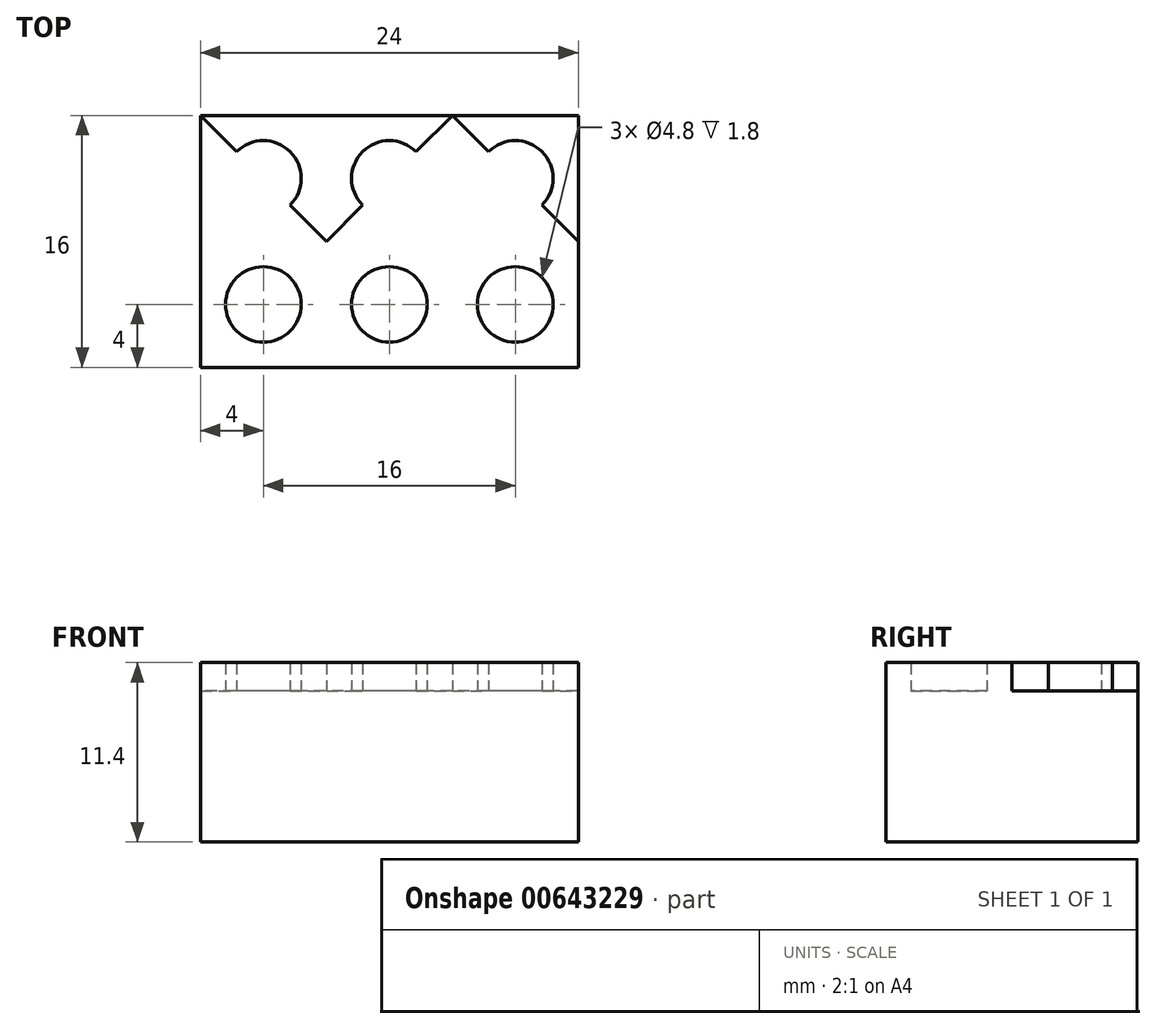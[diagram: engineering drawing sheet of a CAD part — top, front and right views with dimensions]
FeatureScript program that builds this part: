
annotation { "Feature Type Name" : "Feature", "Feature Type Description" : "" }
export const myFeature = defineFeature(function(context is Context, id is Id, definition is map)
    precondition{}
    {
        {
            var Q0;
            Q0=qCreatedBy(makeId("Top.planeOp"),FACE);
            var sketch = newSketch(context, id + "F0", { "sketchPlane" : qUnion([Q0])});
            skLineSegment(sketch, "E0.bottom", {"start": v(0, 0) * mm, "end": v(-24, 0) * mm});
            skLineSegment(sketch, "E0.top", {"start": v(0, 16) * mm, "end": v(-24, 16) * mm});
            skLineSegment(sketch, "E0.left", {"start": v(0, 0) * mm, "end": v(0, 16) * mm});
            skLineSegment(sketch, "E0.right", {"start": v(-24, 0) * mm, "end": v(-24, 16) * mm});
            skSolve(sketch);
        }
        {
            var Q0;
            Q0=makeQuery(id+"F0.imprint","IMPRINT",FACE,{"disambiguationData":[TD([[makeQuery(id+"F0.imprint","IMPRINT",EDGE,{"derivedFrom":sQuery(id+"F0.wireOp",EDGE,"E0.bottom")}),-1.0]])]});
            extrude(context, id + "F1", {"entities" : qUnion([Q0]), "depth" : 9.6 * mm, "offsetDistance" : 25.4 * mm});
        }
        {
            var Q0;
            Q0=makeQuery(id+"F1.opExtrude","CAP_FACE",FACE,{"disambiguationData":[OSD([sQuery(id+"F0.wireOp",EDGE,"E0.bottom"),sQuery(id+"F0.wireOp",EDGE,"E0.top"),sQuery(id+"F0.wireOp",EDGE,"E0.left"),sQuery(id+"F0.wireOp",EDGE,"E0.right")])],"isStart":false});
            var sketch = newSketch(context, id + "F2", { "sketchPlane" : qUnion([Q0])});
            skLineSegment(sketch, "E1", {"start": v(-24, 8) * mm, "end": v(0, 8) * mm, "construction": true});
            skLineSegment(sketch, "E2", {"start": v(-8, 16) * mm, "end": v(-8, 0) * mm, "construction": true});
            skLineSegment(sketch, "E3", {"start": v(-16, 16) * mm, "end": v(-16, 0) * mm, "construction": true});
            skLineSegment(sketch, "E4", {"start": v(-24, 16) * mm, "end": v(-16, 8) * mm});
            skLineSegment(sketch, "E5", {"start": v(-16, 8) * mm, "end": v(-8, 16) * mm});
            skLineSegment(sketch, "E6", {"start": v(-8, 16) * mm, "end": v(0, 8) * mm});
            skCircle(sketch, "E7", {"center": v(-20, 12) * mm, "radius": 2.4 * mm});
            skCircle(sketch, "E8", {"center": v(-12, 12) * mm, "radius": 2.4 * mm});
            skCircle(sketch, "E9", {"center": v(-4, 12) * mm, "radius": 2.4 * mm});
            skCircle(sketch, "E10.MirrorC", {"center": v(-20, 4) * mm, "radius": 2.4 * mm});
            skCircle(sketch, "E11.MirrorC", {"center": v(-12, 4) * mm, "radius": 2.4 * mm});
            skCircle(sketch, "E12.MirrorC", {"center": v(-4, 4) * mm, "radius": 2.4 * mm});
            skSolve(sketch);
        }
        {
            var Q0;
            {var subQ0=sQuery(id+"F2.wireOp",EDGE,"E7");var subQ1=sQuery(id+"F2.wireOp",EDGE,"E4");var subQ2=makeQuery(id+"F2.imprint","INTERSECT",VERTEX,{"disambiguationData":[OD(0.0)],"derivedFrom":[subQ1,subQ0]});Q0=makeQuery(id+"F2.imprint","IMPRINT",FACE,{"disambiguationData":[TD([[makeQuery(id+"F2.imprint","IMPRINT",EDGE,{"disambiguationData":[TD([[subQ2,-1.0]])],"derivedFrom":subQ1}),-1.0]])]});}
            var Q1;
            {var subQ0=sQuery(id+"F2.wireOp",EDGE,"E7");var subQ1=sQuery(id+"F2.wireOp",EDGE,"E4");var subQ2=makeQuery(id+"F2.imprint","INTERSECT",VERTEX,{"disambiguationData":[OD(0.0)],"derivedFrom":[subQ1,subQ0]});Q1=makeQuery(id+"F2.imprint","IMPRINT",FACE,{"disambiguationData":[TD([[makeQuery(id+"F2.imprint","IMPRINT",EDGE,{"disambiguationData":[TD([[subQ2,-1.0]])],"derivedFrom":subQ1}),1.0]])]});}
            var Q2;
            {var subQ0=sQuery(id+"F2.wireOp",EDGE,"E8");var subQ1=sQuery(id+"F2.wireOp",EDGE,"E5");var subQ2=makeQuery(id+"F2.imprint","INTERSECT",VERTEX,{"disambiguationData":[OD(0.0)],"derivedFrom":[subQ1,subQ0]});Q2=makeQuery(id+"F2.imprint","IMPRINT",FACE,{"disambiguationData":[TD([[makeQuery(id+"F2.imprint","IMPRINT",EDGE,{"disambiguationData":[TD([[subQ2,-1.0]])],"derivedFrom":subQ1}),1.0]])]});}
            var Q3;
            {var subQ0=sQuery(id+"F2.wireOp",EDGE,"E8");var subQ1=sQuery(id+"F2.wireOp",EDGE,"E5");var subQ2=makeQuery(id+"F2.imprint","INTERSECT",VERTEX,{"disambiguationData":[OD(0.0)],"derivedFrom":[subQ1,subQ0]});Q3=makeQuery(id+"F2.imprint","IMPRINT",FACE,{"disambiguationData":[TD([[makeQuery(id+"F2.imprint","IMPRINT",EDGE,{"disambiguationData":[TD([[subQ2,-1.0]])],"derivedFrom":subQ1}),-1.0]])]});}
            var Q4;
            {var subQ0=sQuery(id+"F2.wireOp",EDGE,"E9");var subQ1=sQuery(id+"F2.wireOp",EDGE,"E6");var subQ2=makeQuery(id+"F2.imprint","INTERSECT",VERTEX,{"disambiguationData":[OD(0.0)],"derivedFrom":[subQ1,subQ0]});Q4=makeQuery(id+"F2.imprint","IMPRINT",FACE,{"disambiguationData":[TD([[makeQuery(id+"F2.imprint","IMPRINT",EDGE,{"disambiguationData":[TD([[subQ2,-1.0]])],"derivedFrom":subQ1}),1.0]])]});}
            var Q5;
            {var subQ0=sQuery(id+"F2.wireOp",EDGE,"E9");var subQ1=sQuery(id+"F2.wireOp",EDGE,"E6");var subQ2=makeQuery(id+"F2.imprint","INTERSECT",VERTEX,{"disambiguationData":[OD(0.0)],"derivedFrom":[subQ1,subQ0]});Q5=makeQuery(id+"F2.imprint","IMPRINT",FACE,{"disambiguationData":[TD([[makeQuery(id+"F2.imprint","IMPRINT",EDGE,{"disambiguationData":[TD([[subQ2,-1.0]])],"derivedFrom":subQ1}),-1.0]])]});}
            var Q6;
            Q6=makeQuery(id+"F2.imprint","IMPRINT",FACE,{"disambiguationData":[TD([[makeQuery(id+"F2.imprint","IMPRINT",EDGE,{"derivedFrom":sQuery(id+"F2.wireOp",EDGE,"E11.MirrorC")}),-1.0]])]});
            var Q7;
            Q7=makeQuery(id+"F2.imprint","IMPRINT",FACE,{"disambiguationData":[TD([[makeQuery(id+"F2.imprint","IMPRINT",EDGE,{"derivedFrom":sQuery(id+"F2.wireOp",EDGE,"E12.MirrorC")}),-1.0]])]});
            var Q8;
            Q8=makeQuery(id+"F2.imprint","IMPRINT",FACE,{"disambiguationData":[TD([[makeQuery(id+"F2.imprint","IMPRINT",EDGE,{"derivedFrom":sQuery(id+"F2.wireOp",EDGE,"E10.MirrorC")}),-1.0]])]});
            extrude(context, id + "F3", {"entities" : qUnion([Q0, Q1, Q2, Q3, Q4, Q5, Q6, Q7, Q8]), "operationType" : NewBodyOperationType.ADD, "depth" : 1.8 * mm, "offsetDistance" : 25.4 * mm});
        }
    });
